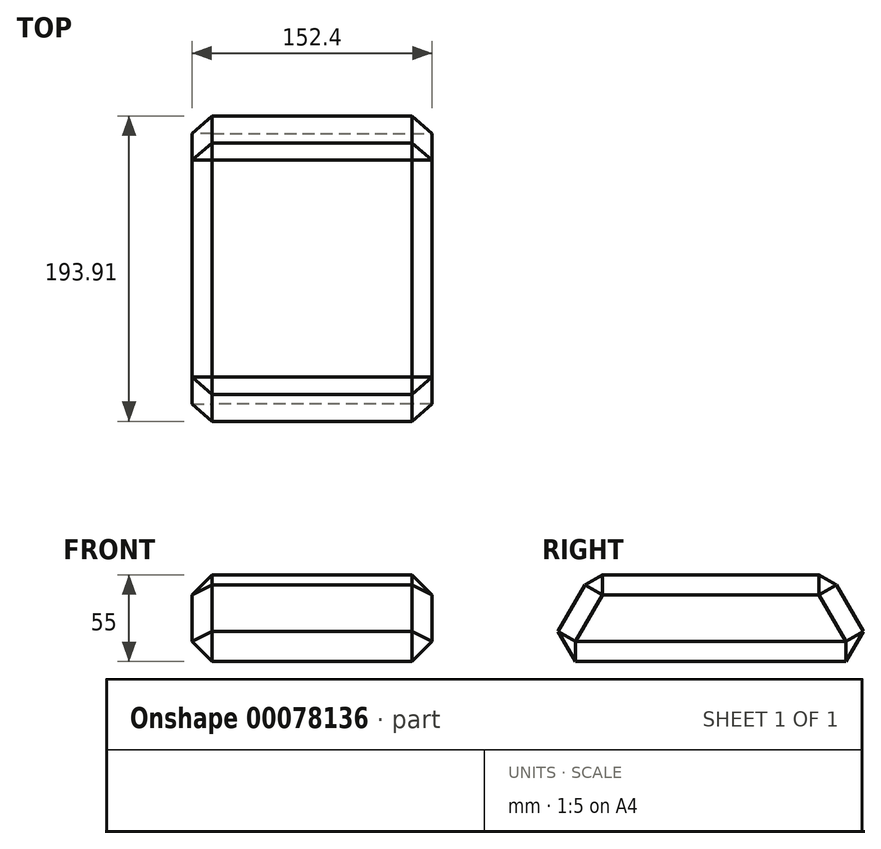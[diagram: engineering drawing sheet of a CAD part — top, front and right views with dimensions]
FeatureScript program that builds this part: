
annotation { "Feature Type Name" : "Feature", "Feature Type Description" : "" }
export const myFeature = defineFeature(function(context is Context, id is Id, definition is map)
    precondition{}
    {
        {
            var Q0;
            Q0=qCreatedBy(makeId("Right.planeOp"),FACE);
            var sketch = newSketch(context, id + "F0", { "sketchPlane" : qUnion([Q0])});
            skLineSegment(sketch, "E0", {"start": v(-42.58, 26.52) * mm, "end": v(-10.83, -28.48) * mm});
            skLineSegment(sketch, "E1", {"start": v(-194.98, 26.52) * mm, "end": v(-42.58, 26.52) * mm});
            skLineSegment(sketch, "E2", {"start": v(-10.83, -28.48) * mm, "end": v(-226.73, -28.48) * mm});
            skLineSegment(sketch, "E3", {"start": v(-194.98, 26.52) * mm, "end": v(-226.73, -28.48) * mm});
            skSolve(sketch);
        }
        {
            var Q0;
            Q0=makeQuery(id+"F0.imprint","IMPRINT",FACE,{"disambiguationData":[TD([[makeQuery(id+"F0.imprint","IMPRINT",EDGE,{"derivedFrom":sQuery(id+"F0.wireOp",EDGE,"E0")}),-1.0]])]});
            var Q1;
            Q1=makeQuery(id+"F0.imprint","IMPRINT",FACE,{"disambiguationData":[TD([[makeQuery(id+"F0.imprint","IMPRINT",EDGE,{"derivedFrom":sQuery(id+"F0.wireOp",EDGE,"E1")}),1.0]])]});
            extrude(context, id + "F1", {"entities" : qUnion([Q0, Q1]), "depth" : 152.4 * mm});
        }
        {
            var Q0;
            Q0=makeQuery(id+"F1.opExtrude","SWEPT_FACE",FACE,{"disambiguationData":[OSD([sQuery(id+"F0.wireOp",EDGE,"f72c8fbd-f3d6-4719-8f9b-d3c11c3248ab0.MirrorCS")])]});
            var Q1;
            Q1=makeQuery(id+"F1.opExtrude","CAP_FACE",FACE,{"disambiguationData":[OSD([sQuery(id+"F0.wireOp",EDGE,"E0"),sQuery(id+"F0.wireOp",EDGE,"E2"),sQuery(id+"F0.wireOp",EDGE,"E3"),sQuery(id+"F0.wireOp",EDGE,"d5ecf617-dce5-4fff-bc88-01f8c2a0c3930.MirrorCS"),sQuery(id+"F0.wireOp",EDGE,"f72c8fbd-f3d6-4719-8f9b-d3c11c3248ab0.MirrorCS"),sQuery(id+"F0.wireOp",EDGE,"2877c025-b2cb-4d48-8635-fdd98e43f8490.MirrorCS")])],"isStart":false});
            var Q2;
            Q2=makeQuery(id+"F1.opExtrude","SWEPT_FACE",FACE,{"disambiguationData":[OSD([sQuery(id+"F0.wireOp",EDGE,"E0")])]});
            var Q3;
            Q3=makeQuery(id+"F1.opExtrude","SWEPT_FACE",FACE,{"disambiguationData":[OSD([sQuery(id+"F0.wireOp",EDGE,"d5ecf617-dce5-4fff-bc88-01f8c2a0c3930.MirrorCS")])]});
            var Q4;
            Q4=makeQuery(id+"F1.opExtrude","CAP_FACE",FACE,{"disambiguationData":[OSD([sQuery(id+"F0.wireOp",EDGE,"E0"),sQuery(id+"F0.wireOp",EDGE,"E2"),sQuery(id+"F0.wireOp",EDGE,"E3"),sQuery(id+"F0.wireOp",EDGE,"d5ecf617-dce5-4fff-bc88-01f8c2a0c3930.MirrorCS"),sQuery(id+"F0.wireOp",EDGE,"f72c8fbd-f3d6-4719-8f9b-d3c11c3248ab0.MirrorCS"),sQuery(id+"F0.wireOp",EDGE,"2877c025-b2cb-4d48-8635-fdd98e43f8490.MirrorCS")])],"isStart":true});
            var Q5;
            Q5=makeQuery(id+"F1.opExtrude","SWEPT_FACE",FACE,{"disambiguationData":[OSD([sQuery(id+"F0.wireOp",EDGE,"2877c025-b2cb-4d48-8635-fdd98e43f8490.MirrorCS")])]});
            var Q6;
            Q6=makeQuery(id+"F1.opExtrude","SWEPT_FACE",FACE,{"disambiguationData":[OSD([sQuery(id+"F0.wireOp",EDGE,"E3")])]});
            chamfer(context, id + "F2", {"entities" : qUnion([Q0, Q1, Q2, Q3, Q4, Q5, Q6]), "width" : 12.7 * mm, "tangentPropagation" : true});
        }
    });
